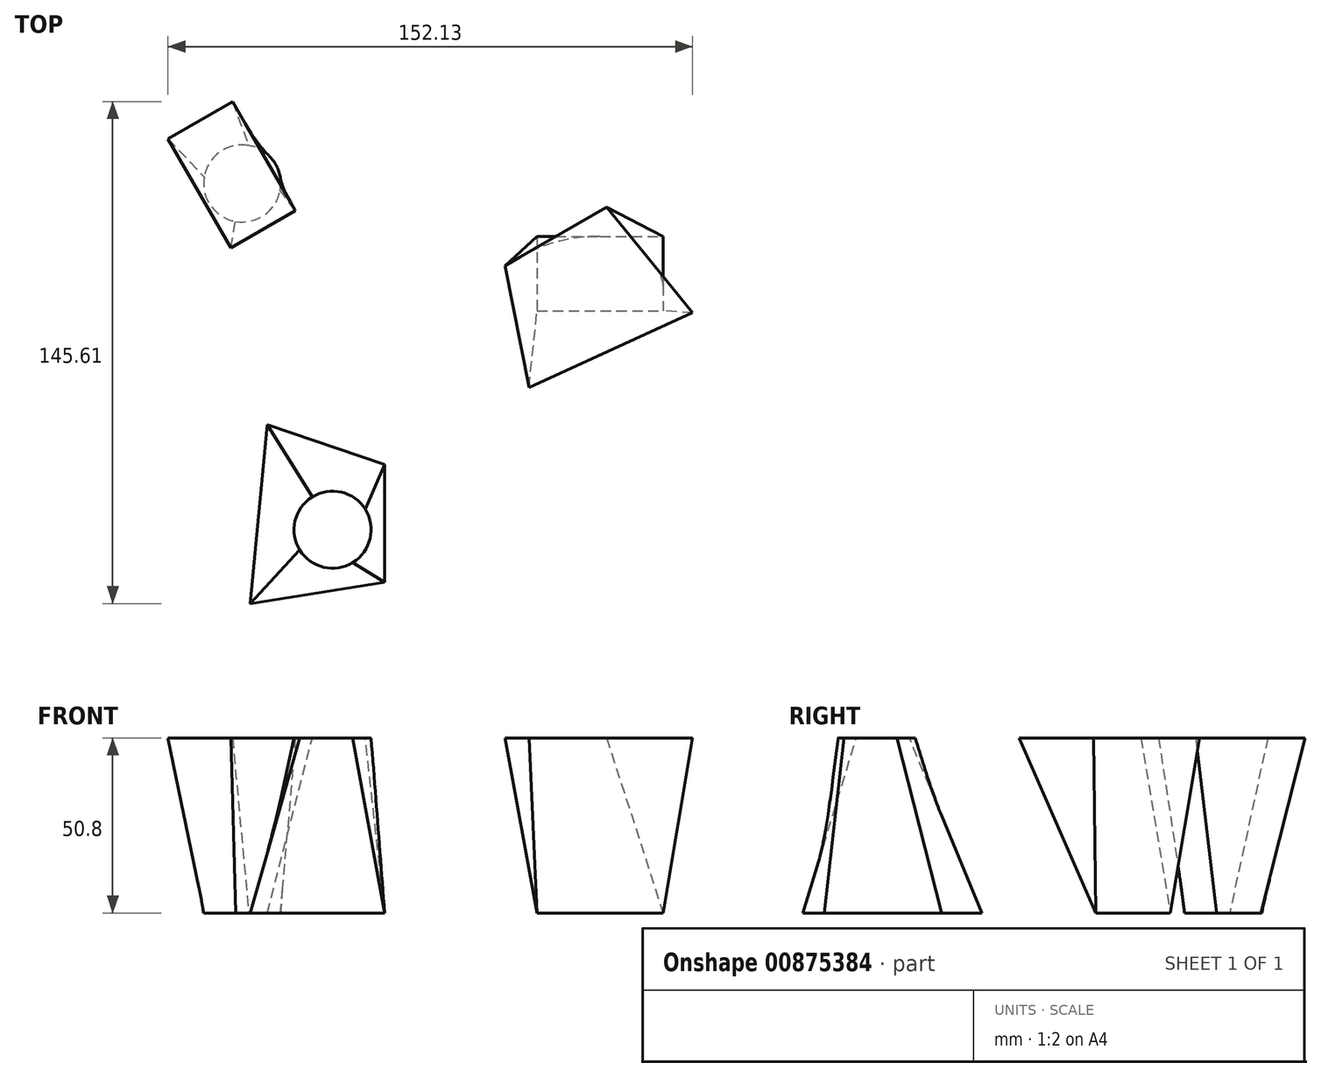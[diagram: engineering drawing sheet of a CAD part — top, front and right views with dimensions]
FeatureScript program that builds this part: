
annotation { "Feature Type Name" : "Feature", "Feature Type Description" : "" }
export const myFeature = defineFeature(function(context is Context, id is Id, definition is map)
    precondition{}
    {
        {
            var Q0;
            Q0=qCreatedBy(makeId("Top.planeOp"),FACE);
            var sketch = newSketch(context, id + "F0", { "sketchPlane" : qUnion([Q0])});
            skCircle(sketch, "E0", {"center": v(-62.28, 52.52) * mm, "radius": 11.18 * mm});
            skLineSegment(sketch, "E1.bottom", {"start": v(23.25, 37.16) * mm, "end": v(59.79, 37.16) * mm});
            skLineSegment(sketch, "E1.top", {"start": v(23.25, 15.57) * mm, "end": v(59.79, 15.57) * mm});
            skLineSegment(sketch, "E1.left", {"start": v(23.25, 37.16) * mm, "end": v(23.25, 15.57) * mm});
            skLineSegment(sketch, "E1.right", {"start": v(59.79, 37.16) * mm, "end": v(59.79, 15.57) * mm});
            skLineSegment(sketch, "E2", {"start": v(-55, -17.45) * mm, "end": v(-20.95, -29.08) * mm});
            skLineSegment(sketch, "E3", {"start": v(-20.95, -29.08) * mm, "end": v(-20.95, -63.13) * mm});
            skLineSegment(sketch, "E4", {"start": v(-20.95, -63.13) * mm, "end": v(-59.98, -69.35) * mm});
            skLineSegment(sketch, "E5", {"start": v(-59.98, -69.35) * mm, "end": v(-55, -17.45) * mm});
            skLineSegment(sketch, "E6", {"start": v(-82.91, 71.7) * mm, "end": v(-82.91, 30.26) * mm, "construction": true});
            skSolve(sketch);
        }
        {
            var Q0;
            Q0=qCreatedBy(makeId("Top.planeOp"),FACE);
            cPlane(context, id + "F1", {"entities" : qUnion([Q0]), "cplaneType" : CPlaneType.OFFSET, "offset" : 50.8 * mm, "width" : 152.4 * mm, "height" : 152.4 * mm});
        }
        {
            var Q0;
            Q0=qCreatedBy(id+"F1.planeOp",FACE);
            var sketch = newSketch(context, id + "F2", { "sketchPlane" : qUnion([Q0])});
            skCircle(sketch, "E7.0", {"center": v(-36.07, -47.94) * mm, "radius": 11.18 * mm});
            skLineSegment(sketch, "E7.1.0", {"start": v(-65.53, 33.82) * mm, "end": v(-46.83, 44.61) * mm});
            skLineSegment(sketch, "E7.1.1", {"start": v(-46.83, 44.61) * mm, "end": v(-65.1, 76.26) * mm});
            skLineSegment(sketch, "E7.1.2", {"start": v(-65.1, 76.26) * mm, "end": v(-83.8, 65.46) * mm});
            skLineSegment(sketch, "E7.1.3", {"start": v(-83.8, 65.46) * mm, "end": v(-65.53, 33.82) * mm});
            skLineSegment(sketch, "E7.2.0", {"start": v(20.9, -6.64) * mm, "end": v(68.33, 15) * mm});
            skLineSegment(sketch, "E7.2.1", {"start": v(68.33, 15) * mm, "end": v(43.42, 45.68) * mm});
            skLineSegment(sketch, "E7.2.2", {"start": v(43.42, 45.68) * mm, "end": v(13.94, 28.66) * mm});
            skLineSegment(sketch, "E7.2.3", {"start": v(13.94, 28.66) * mm, "end": v(20.9, -6.64) * mm});
            skSolve(sketch);
        }
        {
            var Q0;
            Q0=makeQuery(id+"F0.imprint","IMPRINT",FACE,{"disambiguationData":[TD([[makeQuery(id+"F0.imprint","IMPRINT",EDGE,{"derivedFrom":sQuery(id+"F0.wireOp",EDGE,"E2")}),-1.0]])]});
            var Q1;
            Q1=makeQuery(id+"F2.imprint","IMPRINT",FACE,{"disambiguationData":[TD([[makeQuery(id+"F2.imprint","IMPRINT",EDGE,{"derivedFrom":sQuery(id+"F2.wireOp",EDGE,"E7.0")}),1.0]])]});
            loft(context, id + "F3", {"sheetProfilesArray" : [{ "sheetProfileEntities" : qUnion([Q0]) }, { "sheetProfileEntities" : qUnion([Q1]) }]});
        }
        {
            var Q0;
            Q0=makeQuery(id+"F2.imprint","IMPRINT",FACE,{"disambiguationData":[TD([[makeQuery(id+"F2.imprint","IMPRINT",EDGE,{"derivedFrom":sQuery(id+"F2.wireOp",EDGE,"E7.1.0")}),1.0]])]});
            var Q1;
            Q1=makeQuery(id+"F0.imprint","IMPRINT",FACE,{"disambiguationData":[TD([[makeQuery(id+"F0.imprint","IMPRINT",EDGE,{"derivedFrom":sQuery(id+"F0.wireOp",EDGE,"E0")}),1.0]])]});
            loft(context, id + "F4", {"sheetProfilesArray" : [{ "sheetProfileEntities" : qUnion([Q0]) }, { "sheetProfileEntities" : qUnion([Q1]) }]});
        }
        {
            var Q0;
            Q0=makeQuery(id+"F2.imprint","IMPRINT",FACE,{"disambiguationData":[TD([[makeQuery(id+"F2.imprint","IMPRINT",EDGE,{"derivedFrom":sQuery(id+"F2.wireOp",EDGE,"E7.2.0")}),1.0]])]});
            var Q1;
            Q1=makeQuery(id+"F0.imprint","IMPRINT",FACE,{"disambiguationData":[TD([[makeQuery(id+"F0.imprint","IMPRINT",EDGE,{"derivedFrom":sQuery(id+"F0.wireOp",EDGE,"E1.bottom")}),-1.0]])]});
            loft(context, id + "F5", {"sheetProfilesArray" : [{ "sheetProfileEntities" : qUnion([Q0]) }, { "sheetProfileEntities" : qUnion([Q1]) }]});
        }
    });
